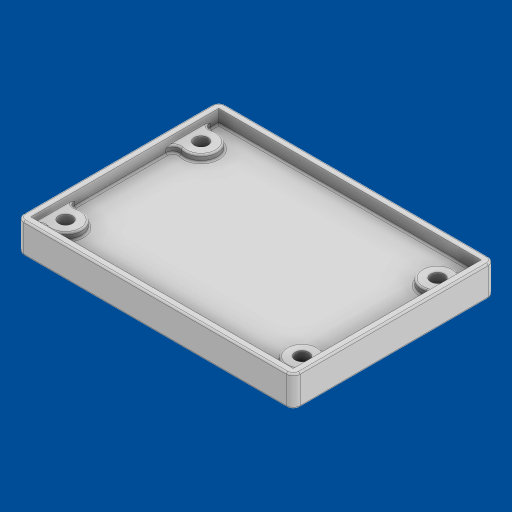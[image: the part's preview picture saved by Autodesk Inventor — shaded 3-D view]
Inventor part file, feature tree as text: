
AUTODESK INVENTOR PART (.ipt)
format: ipt  version: 2023.2 (Build 272271000, 271)  size: 282,624 bytes
history: native  units: mm
features: extrude x3, fillet x3, sketch x2, hole x1
ambient origin geometry x8: Origin, YZ Plane, XZ Plane, XY Plane, X Axis, Y Axis, Z Axis, Center Point
bodies: Solid1 (feature_tree)
feature tree (9):
  sketch  "Sketch1"  dims[d0=77.0mm d1=55.0mm]
  extrude  "Extrusion1"  Depth=55.0mm
  extrude  "Extrusion2"  Depth=0.5mm
  extrude  "Extrusion3"  Depth=0.5mm
  hole  "Hole1"  [1 undecoded]
  fillet  "Fillet1"  Radius=0.25mm
  fillet  "Fillet2"  Radius=2.0mm
  fillet  "Fillet3"  Radius=4.0mm
  sketch  "Sketch2"  dims[d2=69.8mm d3=40.0mm d4=3.57mm d5=4.4mm d6=0.25mm d7=2.0mm d8=4.0mm d9=0.0mm d10=5.0mm d11=0.0mm d12=3.0mm d13=3.0mm d14=3.0mm d15=3.0mm d16=2.0mm d17=0.0mm d18=4.0386mm d19=6.0mm d20=4.0mm d21=2.0mm d22=90.0deg d23=4.5mm d24=0.0mm d25=2.0mm d26=2.0mm d27=0.5mm]
note: 1 required parameter value undecoded (feature->parameter linkage not recoverable at this tier; creation-order binding heuristic only, values carry confidence <= 0.55)
